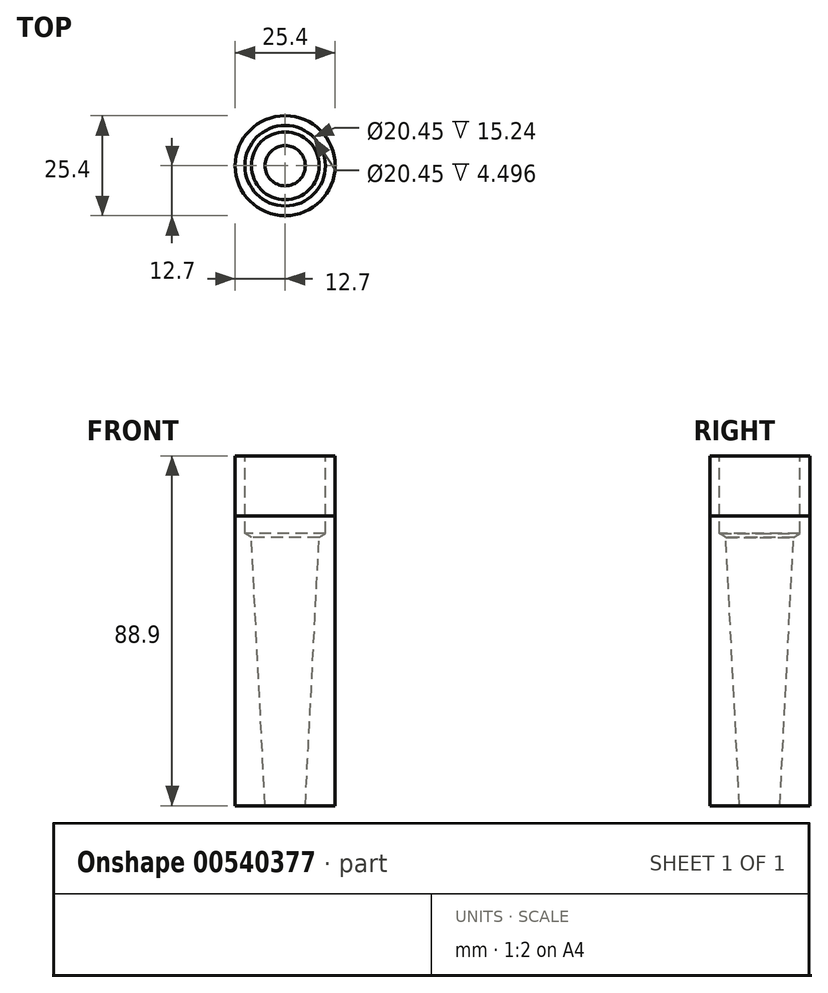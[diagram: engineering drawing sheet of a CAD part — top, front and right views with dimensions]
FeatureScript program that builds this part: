
annotation { "Feature Type Name" : "Feature", "Feature Type Description" : "" }
export const myFeature = defineFeature(function(context is Context, id is Id, definition is map)
    precondition{}
    {
        {
            var Q0;
            Q0=qCreatedBy(makeId("Top.planeOp"),FACE);
            var sketch = newSketch(context, id + "F0", { "sketchPlane" : qUnion([Q0])});
            skCircle(sketch, "E0", {"center": v(0, 0) * mm, "radius": 12.7 * mm});
            skSolve(sketch);
        }
        {
            var Q0;
            Q0=makeQuery(id+"F0.imprint","IMPRINT",FACE,{"disambiguationData":[TD([[makeQuery(id+"F0.imprint","IMPRINT",EDGE,{"derivedFrom":sQuery(id+"F0.wireOp",EDGE,"E0")}),1.0]])]});
            extrude(context, id + "F1", {"entities" : qUnion([Q0]), "depth" : 73.66 * mm, "offsetDistance" : 25.4 * mm, "hasDraft" : true, "draftAngle" : 0 * degree});
        }
        {
            var Q0;
            Q0=qCreatedBy(makeId("Top.planeOp"),FACE);
            var sketch = newSketch(context, id + "F2", { "sketchPlane" : qUnion([Q0])});
            skCircle(sketch, "E1", {"center": v(0, 0) * mm, "radius": 5.11 * mm});
            skSolve(sketch);
        }
        {
            var Q0;
            Q0=makeQuery(id+"F2.imprint","IMPRINT",FACE,{"disambiguationData":[TD([[makeQuery(id+"F2.imprint","IMPRINT",EDGE,{"derivedFrom":sQuery(id+"F2.wireOp",EDGE,"E1")}),1.0]])]});
            extrude(context, id + "F3", {"entities" : qUnion([Q0]), "operationType" : NewBodyOperationType.REMOVE, "endBound" : BoundingType.THROUGH_ALL, "depth" : 25.4 * mm, "offsetDistance" : 25.4 * mm, "hasDraft" : true, "draftAngle" : 2.94 * degree});
        }
        {
            var Q0;
            Q0=makeQuery(id+"F1.opExtrude","CAP_FACE",FACE,{"disambiguationData":[OSD([sQuery(id+"F0.wireOp",EDGE,"E0")])],"isStart":false});
            var sketch = newSketch(context, id + "F4", { "sketchPlane" : qUnion([Q0])});
            skCircle(sketch, "E2", {"center": v(0, 0) * mm, "radius": 12.7 * mm});
            skSolve(sketch);
        }
        {
            var Q0;
            Q0=qSketchRegion(id+"F4",true);
            extrude(context, id + "F5", {"entities" : qUnion([Q0]), "depth" : 15.24 * mm, "offsetDistance" : 25.4 * mm});
        }
        {
            var Q0;
            Q0=makeQuery(id+"F5.opExtrude","CAP_FACE",FACE,{"disambiguationData":[OSD([sQuery(id+"F4.wireOp",EDGE,"E2")])],"isStart":false});
            cPlane(context, id + "F6", {"entities" : qUnion([Q0]), "cplaneType" : CPlaneType.OFFSET, "offset" : 0 * mm, "width" : 152.4 * mm, "height" : 152.4 * mm});
        }
        {
            var Q0;
            Q0=qCreatedBy(id+"F6.planeOp",FACE);
            var sketch = newSketch(context, id + "F7", { "sketchPlane" : qUnion([Q0])});
            skPoint(sketch, "E3", {"position": v(0, 0) * mm});
            skSolve(sketch);
        }
        {
            var Q0;
            Q0=sQuery(id+"F7.wireOp",VERTEX,"E3");
            var Q1;
            Q1=makeQuery(id+"F1.opExtrude","SWEPT_BODY",BODY,{"disambiguationData":[OSD([sQuery(id+"F0.wireOp",EDGE,"E0")])]});
            var Q2;
            Q2=makeQuery(id+"F5.opExtrude","SWEPT_BODY",BODY,{"disambiguationData":[OSD([sQuery(id+"F4.wireOp",EDGE,"E2")])]});
            hole(context, id + "F8", {"style" : HoleStyle.SIMPLE, "endStyle" : HoleEndStyle.BLIND, "holeDiameter" : 20.45 * mm, "holeDepth" : 19.74 * mm, "isTappedThrough" : true, "tappedDepth" : 15.24 * mm, "tapClearance" : 3, "startFromSketch" : true, "locations" : qUnion([Q0]), "scope" : qUnion([Q1, Q2])});
        }
    });
